# Revit family: Pump_Commercial-Effluent-Zoeller-X160_Non_Automatic_Series
name_source: partatom
category: Mechanical Equipment
units: mm (PartAtom-declared; Revit-internal decimal feet)

## family parameters
Always vertical = No
Cut with Voids When Loaded = No
OmniClass Number = 23.60.30.21
OmniClass Title = Pumps
Part Type = Normal
Room Calculation Point = No
Round Connector Dimension = Use Radius
Shared = Yes
Work Plane-Based = Yes

## types (16) — shared parameters
Assembly Code = D2010900
Cooling = Oil Filled
Cord Length = 240"
Cord Type = UL listed, 3-wire neoprene cord and plug (1 Ph) or 4-wire cord with no plug (3 Ph)
Default Elevation = 0"
Description = High Head Explosion Proof. X160 Series Explosion-proof submersible effluent or dewatering pumps.
Discharge Diameter = 1-1/2" NPT (optional 2" or 3" flange)
Discharge Height = 6"
Discharge Radius = 3/4"
Height = 19 5/16"
Hertz = 60
Impeller = Bronze
Impeller Type = Non-clogging vortex
Installation Type = Floor Mounted
Insulation = Class B
Lead Wires Insulation = Class B
Length = 12 3/4"
Manufacturer = Zoeller
Material = Cast Iron-Zoeller-Powder Coated Epoxy
Max. Operating Temp. = 130.00 °F
Min. Recommended Fluid Level = 10"
Minimum Head = 60"
Motor = 1/2 HP
Motor Thermal Shutoff (Single Phase Only) = Thermal Overload Sensors With Automatic Reset.
Motor Type = Submersible
Operation = Non-Automatic
Price = Prices may vary. Please consult Manufacturer Representative for most up-to-date price list.
Product Page URL = http://www.zoellerpumps.com
RPM = 3450
Revised Date = 04/23/2024
Shaft Seal = Carbon and Ceramic
Shipping Weight = 80 lbs
Solid Handling = 3/4" Spherical Solids
Square Ring & Gasket = Neoprene
Type Comments = Available in single or double seal designs.
URL = http://www.zoellerpumps.com
Warranty Information = 36 Months (Limited)
Waste Connection = Yes
Width = 8"

## per-type parameters (varying)
| type | Amps | Apparent Load | Flow @ 5' | Maximum Head | Model | Phase | Type | Voltage |
| X161-115V 1Ph | 16 A | 1783 VA | 100 GPM | 672" | X161 | 1 | Permanent Split Capacitor | 115 V |
| X161-230V 1Ph | 8 A | 1725 VA | 100 GPM | 672" | X161 | 1 | Permanent Split Capacitor | 230 V |
| X161-200V 1Ph | 9 A | 1760 VA | 100 GPM | 672" | X161 | 1 | Permanent Split Capacitor | 200 V |
| X161-208V 1Ph | 9 A | 1830 VA | 100 GPM | 672" | X161 | 1 | Permanent Split Capacitor | 208 V |
| X161-200V 3Ph | 6 A | 1280 VA | 100 GPM | 672" | X161 | 3 Ph | 3 Phase | 200 V |
| X161-208V 3Ph | 6 A | 1331 VA | 100 GPM | 672" | X161 | 3 Ph | 3 Phase | 208 V |
| X161-230V 3Ph | 5 A | 1196 VA | 100 GPM | 672" | X161 | 3 Ph | 3 Phase | 230 V |
| X161-460V 3Ph | 3 A | 1334 VA | 100 GPM | 672" | X161 | 3 Ph | 3 Phase | 460 V |
| X163-115V 1Ph | 15 A | 1725 VA | 0 GPM | 792" | X163 | 1 | Permanent Split Capacitor | 115 V |
| X163-230V 1Ph | 8 A | 1725 VA | 61 GPM | 792" | X163 | 1 | Permanent Split Capacitor | 230 V |
| X163-200V 1Ph | 9 A | 1700 VA | 61 GPM | 792" | X163 | 1 | Permanent Split Capacitor | 200 V |
| X163-208V 1Ph | 9 A | 1768 VA | 61 GPM | 792" | X163 | 1 | Permanent Split Capacitor | 208 V |
| X163-200V 3Ph | 6 A | 1200 VA | 61 GPM | 792" | X163 | 3 Ph | 3 Phase | 200 V |
| X163-208V 3Ph | 6 A | 1248 VA | 61 GPM | 792" | X163 | 3 Ph | 3 Phase | 208 V |
| X163-230V 3Ph | 5 A | 1104 VA | 61 GPM | 792" | X163 | 3 Ph | 3 Phase | 230 V |
| X163-460V 3Ph | 3 A | 1334 VA | 61 GPM | 792" | X163 | 3 Ph | 3 Phase | 460 V |

## geometry (parser evidence)
native form markers: Blend x4, Sweep x3
no freeform markers — native parametric forms only
